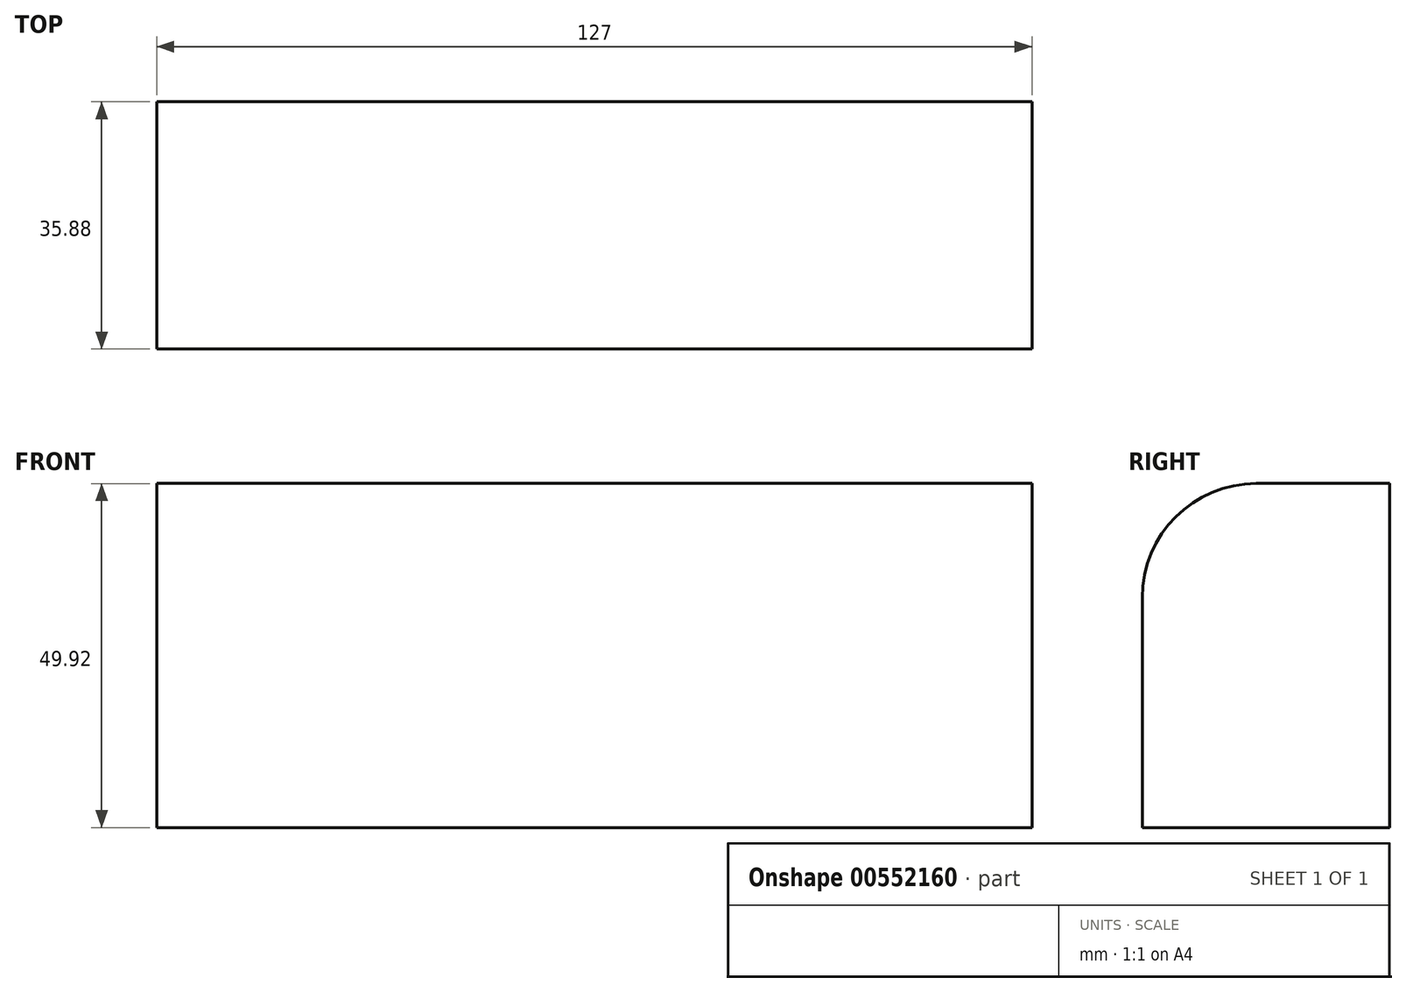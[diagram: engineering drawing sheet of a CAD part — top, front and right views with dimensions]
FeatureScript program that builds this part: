
annotation { "Feature Type Name" : "Feature", "Feature Type Description" : "" }
export const myFeature = defineFeature(function(context is Context, id is Id, definition is map)
    precondition{}
    {
        {
            var Q0;
            Q0=qCreatedBy(makeId("Right.planeOp"),FACE);
            var sketch = newSketch(context, id + "F0", { "sketchPlane" : qUnion([Q0])});
            skLineSegment(sketch, "E0", {"start": v(-106.12, 114.77) * mm, "end": v(-20.47, 43.06) * mm});
            skLineSegment(sketch, "E1", {"start": v(-20.47, 43.06) * mm, "end": v(9.1, 56.29) * mm});
            skLineSegment(sketch, "E2", {"start": v(9.1, 56.29) * mm, "end": v(56.1, -6.6) * mm});
            skLineSegment(sketch, "E3", {"start": v(-162.98, 66.6) * mm, "end": v(9.1, -17.24) * mm});
            skLineSegment(sketch, "E4.bottom", {"start": v(94.15, -9.75) * mm, "end": v(130.03, -9.75) * mm});
            skLineSegment(sketch, "E4.top", {"start": v(94.15, -59.67) * mm, "end": v(130.03, -59.67) * mm});
            skLineSegment(sketch, "E4.left", {"start": v(94.15, -9.75) * mm, "end": v(94.15, -59.67) * mm});
            skLineSegment(sketch, "E4.right", {"start": v(130.03, -9.75) * mm, "end": v(130.03, -59.67) * mm});
            skSolve(sketch);
        }
        {
            var Q0;
            Q0 = qSketchRegion(id + "F0", true);
            extrude(context, id + "F1", {"entities" : qUnion([Q0]), "depth" : 127 * mm, "offsetDistance" : 25.4 * mm});
        }
        {
            var Q0;
            Q0=makeQuery(id+"F1.opExtrude","SWEPT_EDGE",EDGE,{"disambiguationData":[OSD([sQuery(id+"F0.wireOp",EDGE,"E4.bottom"),sQuery(id+"F0.wireOp",EDGE,"E4.left")])]});
            fillet(context, id + "F2", {"entities" : qUnion([Q0]), "radius" : 16.56 * mm, "tangentPropagation" : true, "allowEdgeOverflow" : false});
        }
    });
